# Revit family: Naughtone_Tbls_Fold_CircularCoffee
name_source: partatom
category: Furniture
revit_build: Autodesk Revit 2015 (Build: 20160512_1515(x64)
units: mm (PartAtom-declared; Revit-internal decimal feet)

## types (2) — shared parameters
AdditionalMaterials = Additional material and finish options available. Please contact Naughtone direct for further information.
Assembly Code = E2020200
AssetType = Movable
BIMObjectName = Naughtone_Tables_Fold_CircularCoffee
Category = Pr_40_50_21_14 : Coffee Tables
DurationUnit = year
IfcExportAs = IfcFurnishingElementType
IfcExportType = TABLE
Keynote = Pr_40_50_21_14
ManufacturerAddressUK = Knaresborough Tech Park, Manse Lane, Knaresborough, HG5 8LF
ManufacturerName = Naughtone
ManufacturerURL = www.naughtone.com/
Material = Mild Steel
NBSDescription = Tables
NBSReference = 45-35-86/327
Name = Tables_Fold_CircularCoffee_Naughtone
NominalHeight = 350 mm  [stored 1.14829 ft]
ProductInformation = www.naughtone.com/portfolio-view/fold
ScheduleType |RF| = NaughtoneFoldData
Shape = Circular
URL = www.naughtone.com/
Uniclass2015Description = Coffee tables
Uniclass2015Reference = Pr_40_50_21_14
Uniclass2015Version = Products v1.3
Version = 1
WarrantyDescription = Request warranty information from naughtone
WarrantyDurationLabor = 5
WarrantyDurationParts = 5
WarrantyDurationUnit = year
zero-valued in all types: Cost, NumberOfChairs, WorksurfaceArea

## per-type parameters (varying)
| type | 650 | 850 | Description | Model | ModelNumber | ModelReference | NominalLength | NominalWidth |
| 650mmx650mmx350mm | Yes | No | Fold 650mm Diameter Coffee Table | FOLD-650-DIA-LO | FOLD-650-DIA-LO | Fold 650mm Diameter Coffee Table | 650 mm  [stored 2.13255 ft] | 650 mm  [stored 2.13255 ft] |
| 850mmx850mmx350mm | No | Yes | Fold 850mm Diameter Coffee Table | FOLD-850-DIA-LO | FOLD-850-DIA-LO | Fold 850mm Diameter Coffee Table | 850 mm  [stored 2.78871 ft] | 850 mm  [stored 2.78871 ft] |

note: column(s) folded — value = type name in every type: Size

note: [stored X ft] marks values corroborated as IEEE doubles in the binary element streams (Revit-internal decimal feet)

## geometry (parser evidence)
native form markers: Sweep x6
no freeform markers — native parametric forms only
